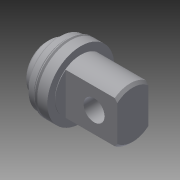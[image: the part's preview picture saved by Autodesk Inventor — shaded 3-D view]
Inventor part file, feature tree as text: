
AUTODESK INVENTOR PART (.ipt)
format: ipt  version: 2014 SP2 (Build 180246200, 246)  size: 228,864 bytes
history: native  units: in
note: dims shown in document units (in); Inventor stores cm internally (conversion verified against a paired STEP export)
features: other x126, sketch x6, revolve x4, extrude x2
ambient origin geometry x8: Origin, YZ Plane, XZ Plane, XY Plane, X Axis, Y Axis, Z Axis, Center Point
bodies: Solid1 (feature_tree)
feature tree (138):
  revolve  "Revolution1"  Angle=360.0deg
  revolve  "Revolution2"  Angle=360.0deg
  revolve  "Revolution3"  [1 undecoded]
  revolve  "Revolution4"  [1 undecoded]
  extrude  "Extrusion1"  [1 undecoded]
  extrude  "Extrusion2"  [1 undecoded]
  other  "1_XY"
  other  "1_YZ"
  other  "1_ZX"
  other  "1_X"
  other  "1_Y"
  other  "1_Z"
  other  "1_Center"
  other  "lovra_XY"
  other  "lovra_YZ"
  other  "lovra_ZX"
  other  "lovra_X"
  other  "lovra_Y"
  other  "lovra_Z"
  other  "lovra_Center"
  other  "lovra1_XY"
  other  "lovra1_YZ"
  other  "lovra1_ZX"
  other  "lovra1_X"
  other  "lovra1_Y"
  other  "lovra1_Z"
  other  "lovra1_Center"
  other  "lovra2_XY"
  other  "lovra2_YZ"
  other  "lovra2_ZX"
  other  "lovra2_X"
  other  "lovra2_Y"
  other  "lovra2_Z"
  other  "lovra2_Center"
  other  "lovra21_XY"
  other  "lovra21_YZ"
  other  "lovra21_ZX"
  other  "lovra21_X"
  other  "lovra21_Y"
  other  "lovra21_Z"
  other  "lovra21_Center"
  other  "lovra22_XY"
  other  "lovra22_YZ"
  other  "lovra22_ZX"
  other  "lovra22_X"
  other  "lovra22_Y"
  other  "lovra22_Z"
  other  "lovra22_Center"
  other  "lovra3_XY"
  other  "lovra3_YZ"
  other  "lovra3_ZX"
  other  "lovra3_X"
  other  "lovra3_Y"
  other  "lovra3_Z"
  other  "lovra3_Center"
  other  "olen_XY"
  other  "olen_YZ"
  other  "olen_ZX"
  other  "olen_X"
  other  "olen_Y"
  other  "olen_Z"
  other  "olen_Center"
  other  "p1_XY"
  other  "p1_YZ"
  other  "p1_ZX"
  other  "p1_X"
  other  "p1_Y"
  other  "p1_Z"
  other  "p1_Center"
  other  "p2_XY"
  other  "p2_YZ"
  other  "p2_ZX"
  other  "p2_X"
  other  "p2_Y"
  other  "p2_Z"
  other  "p2_Center"
  other  "port2_XY"
  other  "port2_YZ"
  other  "port2_ZX"
  other  "port2_X"
  other  "port2_Y"
  other  "port2_Z"
  other  "port2_Center"
  other  "thd1_XY"
  other  "thd1_YZ"
  other  "thd1_ZX"
  other  "thd1_X"
  other  "thd1_Y"
  other  "thd1_Z"
  other  "thd1_Center"
  other  "thd2_XY"
  other  "thd2_YZ"
  other  "thd2_ZX"
  other  "thd2_X"
  other  "thd2_Y"
  other  "thd2_Z"
  other  "thd2_Center"
  other  "to_mounting_bracket_XY"
  other  "to_mounting_bracket_YZ"
  other  "to_mounting_bracket_ZX"
  other  "to_mounting_bracket_X"
  other  "to_mounting_bracket_Y"
  other  "to_mounting_bracket_Z"
  other  "to_mounting_bracket_Center"
  other  "to_nut_XY"
  other  "to_nut_YZ"
  other  "to_nut_ZX"
  other  "to_nut_X"
  other  "to_nut_Y"
  other  "to_nut_Z"
  other  "to_nut_Center"
  other  "to_pin_XY"
  other  "to_pin_YZ"
  other  "to_pin_ZX"
  other  "to_pin_X"
  other  "to_pin_Y"
  other  "to_pin_Z"
  other  "to_pin_Center"
  other  "to_screw_XY"
  other  "to_screw_YZ"
  other  "to_screw_ZX"
  other  "to_screw_X"
  other  "to_screw_Y"
  other  "to_screw_Z"
  other  "to_screw_Center"
  other  "to_tube_XY"
  other  "to_tube_YZ"
  other  "to_tube_ZX"
  other  "to_tube_X"
  other  "to_tube_Y"
  other  "to_tube_Z"
  other  "to_tube_Center"
  sketch  "Sketch_1"  dims[d0=360.0deg d1=360.0deg]
  sketch  "Sketch_24"  dims[d2=360.0deg d3=360.0deg]
  sketch  "Sketch_26"  dims[d4=0.625in d5=0.0in d6=0.745in d7=0.0in]
  sketch  "Sketch_27"  dims[d8=0.0in d9=0.0in d10=0.0in d11=0.0in d12=0.0in d13=0.0in d14=0.0in]
  sketch  "Sketch_28"
  sketch  "Sketch_29"
note: 4 required parameter values undecoded (feature->parameter linkage not recoverable at this tier; creation-order binding heuristic only, values carry confidence <= 0.55)